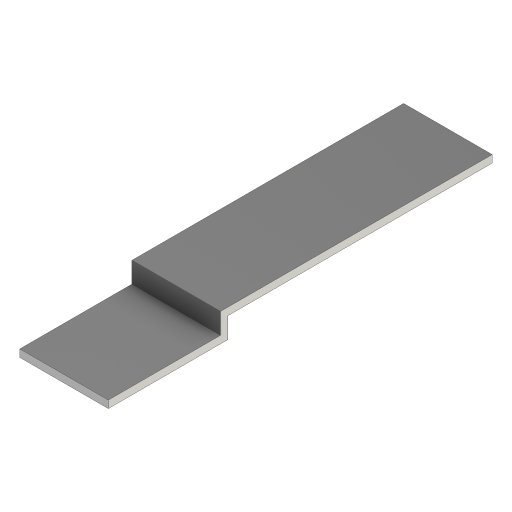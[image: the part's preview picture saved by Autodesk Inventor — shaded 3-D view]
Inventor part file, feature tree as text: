
AUTODESK INVENTOR PART (.ipt)
format: ipt  version: 2023 (Build 270158000, 158)  size: 107,520 bytes
history: native  units: mm
features: extrude x1, plane x1, sketch x1
ambient origin geometry x8: Origin, YZ Plane, XZ Plane, XY Plane, X Axis, Y Axis, Z Axis, Center Point
bodies: 实体1 (feature_tree)
feature tree (3):
  extrude  "拉伸1"  Depth=140.0mm
  plane  "工作平面1"
  sketch  "草图1"  dims[d0=810.0mm d1=140.0mm d2=2600.0mm d3=50.0mm d4=600.0mm d5=0.0mm d6=500.0mm]
